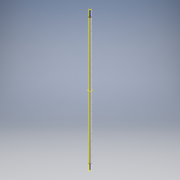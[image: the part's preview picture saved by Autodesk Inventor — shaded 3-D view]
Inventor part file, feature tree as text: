
AUTODESK INVENTOR PART (.ipt)
format: ipt  version: 2017 (Build 210142000, 142)  size: 159,744 bytes
history: native  units: mm
features: extrude x2, sketch x2, pattern_linear x1, projected_geometry x1
ambient origin geometry x8: Origin, YZ Plane, XZ Plane, XY Plane, X Axis, Y Axis, Z Axis, Center Point
bodies: Solid1 (feature_tree)
feature tree (6):
  extrude  "Extrusion1"  Depth=72.0mm
  extrude  "Extrusion2"  Depth=44.0mm
  pattern_linear  "Rectangular Pattern1"  Count1=400 Spacing1=0.0mm
  sketch  "Sketch1"  dims[d0=76.0mm d1=72.0mm]
  sketch  "Sketch2"  dims[d2=2000.0mm d3=0.0mm d4=44.0mm d6=4000.0mm d7=0.0mm d8=190.0mm d10=200.0mm d11=2000.0mm d12=0.0mm d18=200.0mm]
  projected_geometry  "Projected Loop1"
